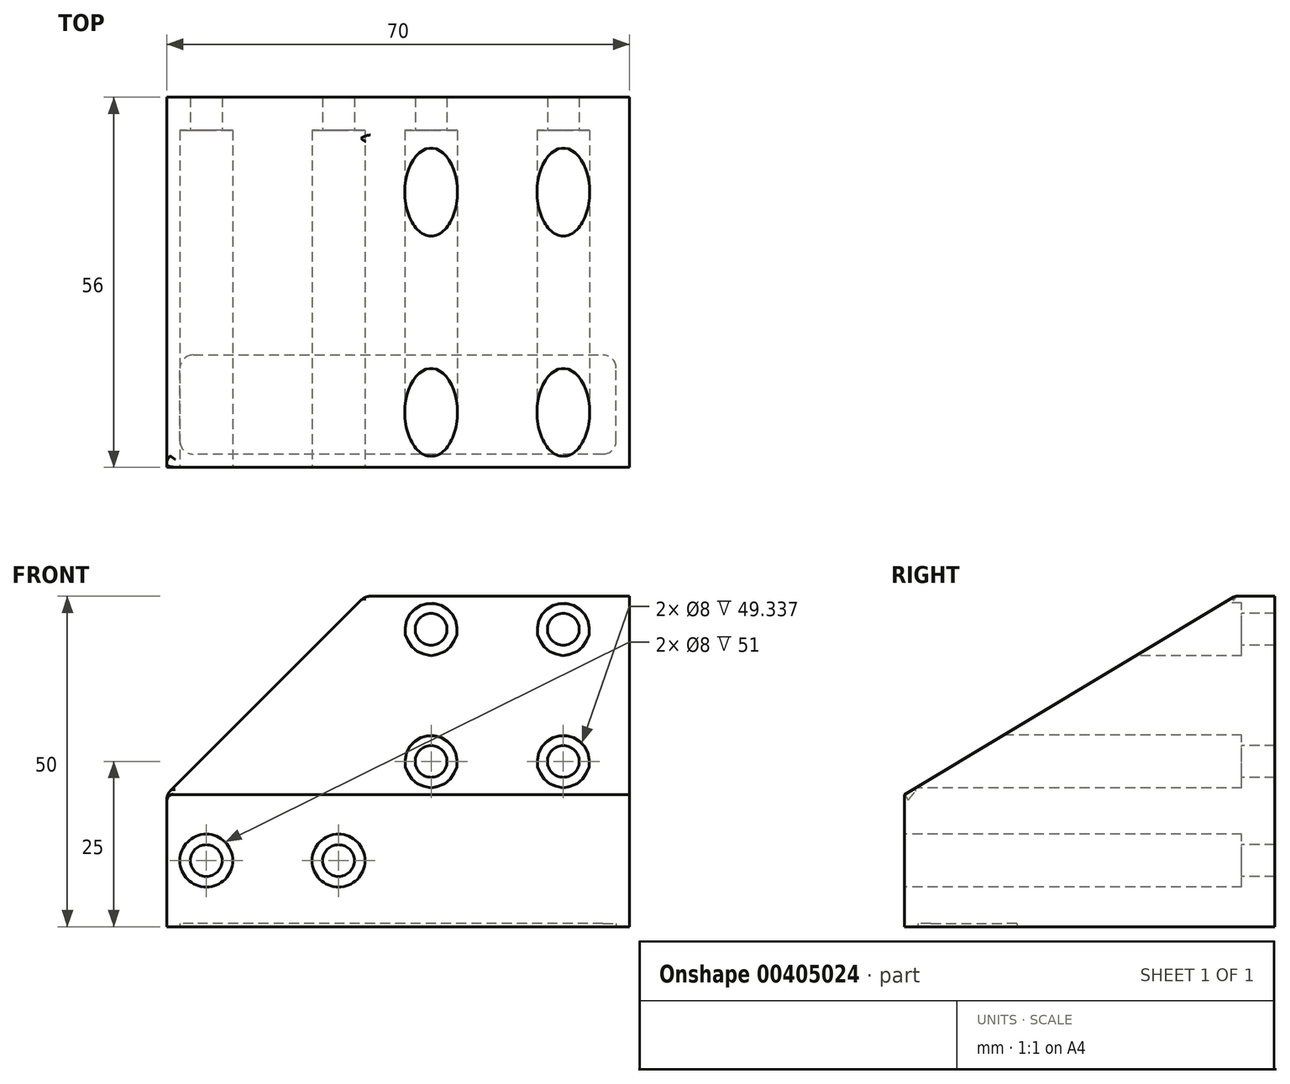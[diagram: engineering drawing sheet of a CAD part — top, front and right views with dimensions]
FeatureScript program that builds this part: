
annotation { "Feature Type Name" : "Feature", "Feature Type Description" : "" }
export const myFeature = defineFeature(function(context is Context, id is Id, definition is map)
    precondition{}
    {
        {
            var Q0;
            Q0=qCreatedBy(makeId("Front.planeOp"),FACE);
            var sketch = newSketch(context, id + "F0", { "sketchPlane" : qUnion([Q0])});
            skLineSegment(sketch, "E0.bottom", {"start": v(0, 0) * mm, "end": v(-70, 0) * mm});
            skLineSegment(sketch, "E0.top", {"start": v(0, 50) * mm, "end": v(-70, 50) * mm});
            skLineSegment(sketch, "E0.left", {"start": v(0, 0) * mm, "end": v(0, 50) * mm});
            skLineSegment(sketch, "E0.right", {"start": v(-70, 0) * mm, "end": v(-70, 50) * mm});
            skSolve(sketch);
        }
        {
            var Q0;
            Q0=makeQuery(id+"F0.imprint","IMPRINT",FACE,{"disambiguationData":[TD([[makeQuery(id+"F0.imprint","IMPRINT",EDGE,{"derivedFrom":sQuery(id+"F0.wireOp",EDGE,"E0.bottom")}),-1.0]])]});
            extrude(context, id + "F1", {"entities" : qUnion([Q0]), "depth" : 56 * mm});
        }
        {
            var Q0;
            Q0=makeQuery(id+"F1.opExtrude","SWEPT_EDGE",EDGE,{"disambiguationData":[OSD([sQuery(id+"F0.wireOp",EDGE,"E0.top"),sQuery(id+"F0.wireOp",EDGE,"E0.right")])]});
            chamfer(context, id + "F2", {"entities" : qUnion([Q0]), "width" : 30 * mm, "tangentPropagation" : true});
        }
        {
            var Q0;
            Q0=qCreatedBy(makeId("Right.planeOp"),FACE);
            var sketch = newSketch(context, id + "F3", { "sketchPlane" : qUnion([Q0])});
            skLineSegment(sketch, "E1", {"start": v(-6, 50) * mm, "end": v(-56, 20) * mm});
            skLineSegment(sketch, "E2", {"start": v(-56, 20) * mm, "end": v(-56, 50) * mm});
            skLineSegment(sketch, "E3", {"start": v(-56, 50) * mm, "end": v(-6, 50) * mm});
            skSolve(sketch);
        }
        {
            var Q0;
            Q0 = qSketchRegion(id + "F3", true);
            extrude(context, id + "F4", {"entities" : qUnion([Q0]), "operationType" : NewBodyOperationType.REMOVE, "endBound" : BoundingType.THROUGH_ALL, "oppositeDirection" : true, "depth" : 25 * mm});
        }
        {
            var Q0;
            Q0=qCreatedBy(makeId("Front.planeOp"),FACE);
            cPlane(context, id + "F5", {"entities" : qUnion([Q0]), "cplaneType" : CPlaneType.OFFSET, "offset" : 56 * mm, "width" : 150 * mm, "height" : 150 * mm});
        }
        {
            var Q0;
            Q0=qCreatedBy(id+"F5.planeOp",FACE);
            var sketch = newSketch(context, id + "F6", { "sketchPlane" : qUnion([Q0])});
            skLineSegment(sketch, "E4", {"start": v(-64, 10) * mm, "end": v(-44, 10) * mm});
            skLineSegment(sketch, "E5", {"start": v(-64, 10) * mm, "end": v(-70, 10) * mm, "construction": true});
            skLineSegment(sketch, "E6.bottom", {"start": v(-30, 45) * mm, "end": v(-10, 45) * mm});
            skLineSegment(sketch, "E6.top", {"start": v(-30, 25) * mm, "end": v(-10, 25) * mm});
            skLineSegment(sketch, "E6.left", {"start": v(-30, 45) * mm, "end": v(-30, 25) * mm});
            skLineSegment(sketch, "E6.right", {"start": v(-10, 45) * mm, "end": v(-10, 25) * mm});
            skSolve(sketch);
        }
        {
            var Q0;
            Q0=sQuery(id+"F6.wireOp",VERTEX,"E4.start");
            var Q1;
            Q1=sQuery(id+"F6.wireOp",VERTEX,"E4.end");
            var Q2;
            Q2=sQuery(id+"F6.wireOp",VERTEX,"E6.bottom.start");
            var Q3;
            Q3=sQuery(id+"F6.wireOp",VERTEX,"E6.top.start");
            var Q4;
            Q4=sQuery(id+"F6.wireOp",VERTEX,"E6.bottom.end");
            var Q5;
            Q5=sQuery(id+"F6.wireOp",VERTEX,"E6.top.end");
            var Q6;
            Q6=makeQuery(id+"F1.opExtrude","SWEPT_BODY",BODY,{"disambiguationData":[OSD([sQuery(id+"F0.wireOp",EDGE,"E0.bottom"),sQuery(id+"F0.wireOp",EDGE,"E0.top"),sQuery(id+"F0.wireOp",EDGE,"E0.left"),sQuery(id+"F0.wireOp",EDGE,"E0.right")])]});
            hole(context, id + "F7", {"style" : HoleStyle.C_BORE, "endStyle" : HoleEndStyle.THROUGH, "holeDiameter" : 4.8 * mm, "cBoreDiameter" : 8 * mm, "cBoreDepth" : 51 * mm, "isTappedThrough" : true, "tappedDepth" : 12 * mm, "tapClearance" : 3, "startFromSketch" : true, "locations" : qUnion([Q0, Q1, Q2, Q3, Q4, Q5]), "scope" : qUnion([Q6])});
        }
        {
            var Q0;
            {var subQ0=sQuery(id+"F0.wireOp",EDGE,"E0.right");Q0=makeQuery(id+"F2.opChamfer","BLEND_EDGE",EDGE,{"blendedFrom":[makeQuery(id+"F1.opExtrude","SWEPT_EDGE",EDGE,{"disambiguationData":[OSD([sQuery(id+"F0.wireOp",EDGE,"E0.top"),subQ0])]}),makeQuery(id+"F1.opExtrude","SWEPT_FACE",FACE,{"disambiguationData":[OSD([subQ0])]})],"blendedInto":[makeQuery(id+"F1.opExtrude","SWEPT_FACE",FACE,{"disambiguationData":[OSD([subQ0])]})]});}
            var Q1;
            Q1=makeQuery(id+"F4.boolean.opBoolean","COPY",EDGE,{"derivedFrom":makeQuery(id+"F4.opExtrude","SWEPT_EDGE",EDGE,{"disambiguationData":[OSD([sQuery(id+"F3.wireOp",EDGE,"E1"),sQuery(id+"F3.wireOp",EDGE,"E2")])]})});
            var Q2;
            {var subQ0=sQuery(id+"F0.wireOp",EDGE,"E0.top");Q2=makeQuery(id+"F2.opChamfer","BLEND_EDGE",EDGE,{"blendedFrom":[makeQuery(id+"F1.opExtrude","SWEPT_EDGE",EDGE,{"disambiguationData":[OSD([subQ0,sQuery(id+"F0.wireOp",EDGE,"E0.right")])]}),makeQuery(id+"F1.opExtrude","SWEPT_FACE",FACE,{"disambiguationData":[OSD([subQ0])]})],"blendedInto":[makeQuery(id+"F1.opExtrude","SWEPT_FACE",FACE,{"disambiguationData":[OSD([subQ0])]})]});}
            var Q3;
            Q3=makeQuery(id+"F4.boolean.opBoolean","COPY",EDGE,{"derivedFrom":makeQuery(id+"F4.opExtrude","SWEPT_EDGE",EDGE,{"disambiguationData":[OSD([sQuery(id+"F3.wireOp",EDGE,"E1"),sQuery(id+"F3.wireOp",EDGE,"E3")])]})});
            fillet(context, id + "F8", {"entities" : qUnion([Q0, Q1, Q2, Q3]), "radius" : 2 * mm, "tangentPropagation" : true, "allowEdgeOverflow" : false});
        }
        {
            var Q0;
            Q0=makeQuery(id+"F4.boolean.opBoolean","INTERSECT",EDGE,{"derivedFrom":[makeQuery(id+"F2.opChamfer","BLEND_FACE",FACE,{"disambiguationData":[OSD([sQuery(id+"F0.wireOp",EDGE,"E0.top"),sQuery(id+"F0.wireOp",EDGE,"E0.right")])]}),makeQuery(id+"F4.opExtrude","SWEPT_FACE",FACE,{"disambiguationData":[OSD([sQuery(id+"F3.wireOp",EDGE,"E1")])]})]});
            var Q1;
            Q1=makeQuery(id+"F4.boolean.opBoolean","COPY",EDGE,{"derivedFrom":makeQuery(id+"F4.opExtrude","CAP_EDGE",EDGE,{"disambiguationData":[OSD([sQuery(id+"F3.wireOp",EDGE,"E1")])],"isStart":true})});
            fillet(context, id + "F9", {"entities" : qUnion([Q0, Q1]), "radius" : 1 * mm, "tangentPropagation" : true, "allowEdgeOverflow" : false});
        }
        {
            var Q0;
            Q0=makeQuery(id+"F1.opExtrude","SWEPT_FACE",FACE,{"disambiguationData":[OSD([sQuery(id+"F0.wireOp",EDGE,"E0.bottom")])]});
            var sketch = newSketch(context, id + "F10", { "sketchPlane" : qUnion([Q0])});
            skLineSegment(sketch, "E7.0", {"start": v(-68, 54) * mm, "end": v(-68, 39) * mm});
            skLineSegment(sketch, "E7.1", {"start": v(-2, 54) * mm, "end": v(-68, 54) * mm});
            skLineSegment(sketch, "E7.2", {"start": v(-2, 54) * mm, "end": v(-2, 39) * mm});
            skLineSegment(sketch, "E8", {"start": v(-68, 39) * mm, "end": v(-2, 39) * mm});
            skSolve(sketch);
        }
        {
            var Q0;
            Q0=makeQuery(id+"F10.imprint","IMPRINT",FACE,{"disambiguationData":[TD([[makeQuery(id+"F10.imprint","IMPRINT",EDGE,{"derivedFrom":sQuery(id+"F10.wireOp",EDGE,"E7.0")}),1.0]])]});
            extrude(context, id + "F11", {"entities" : qUnion([Q0]), "operationType" : NewBodyOperationType.REMOVE, "oppositeDirection" : true, "depth" : 0.5 * mm});
        }
        {
            var Q0;
            Q0=makeQuery(id+"F11.boolean.opBoolean","COPY",EDGE,{"derivedFrom":makeQuery(id+"F11.opExtrude","SWEPT_EDGE",EDGE,{"disambiguationData":[OSD([sQuery(id+"F10.wireOp",EDGE,"E7.1"),sQuery(id+"F10.wireOp",EDGE,"E7.2")])]})});
            var Q1;
            Q1=makeQuery(id+"F11.boolean.opBoolean","COPY",EDGE,{"derivedFrom":makeQuery(id+"F11.opExtrude","SWEPT_EDGE",EDGE,{"disambiguationData":[OSD([sQuery(id+"F10.wireOp",EDGE,"E7.0"),sQuery(id+"F10.wireOp",EDGE,"E7.1")])]})});
            var Q2;
            Q2=makeQuery(id+"F11.boolean.opBoolean","COPY",EDGE,{"derivedFrom":makeQuery(id+"F11.opExtrude","SWEPT_EDGE",EDGE,{"disambiguationData":[OSD([sQuery(id+"F10.wireOp",EDGE,"E7.0"),sQuery(id+"F10.wireOp",EDGE,"E8")])]})});
            var Q3;
            Q3=makeQuery(id+"F11.boolean.opBoolean","COPY",EDGE,{"derivedFrom":makeQuery(id+"F11.opExtrude","SWEPT_EDGE",EDGE,{"disambiguationData":[OSD([sQuery(id+"F10.wireOp",EDGE,"E7.2"),sQuery(id+"F10.wireOp",EDGE,"E8")])]})});
            fillet(context, id + "F12", {"entities" : qUnion([Q0, Q1, Q2, Q3]), "radius" : 2 * mm, "tangentPropagation" : true, "allowEdgeOverflow" : false});
        }
    });
